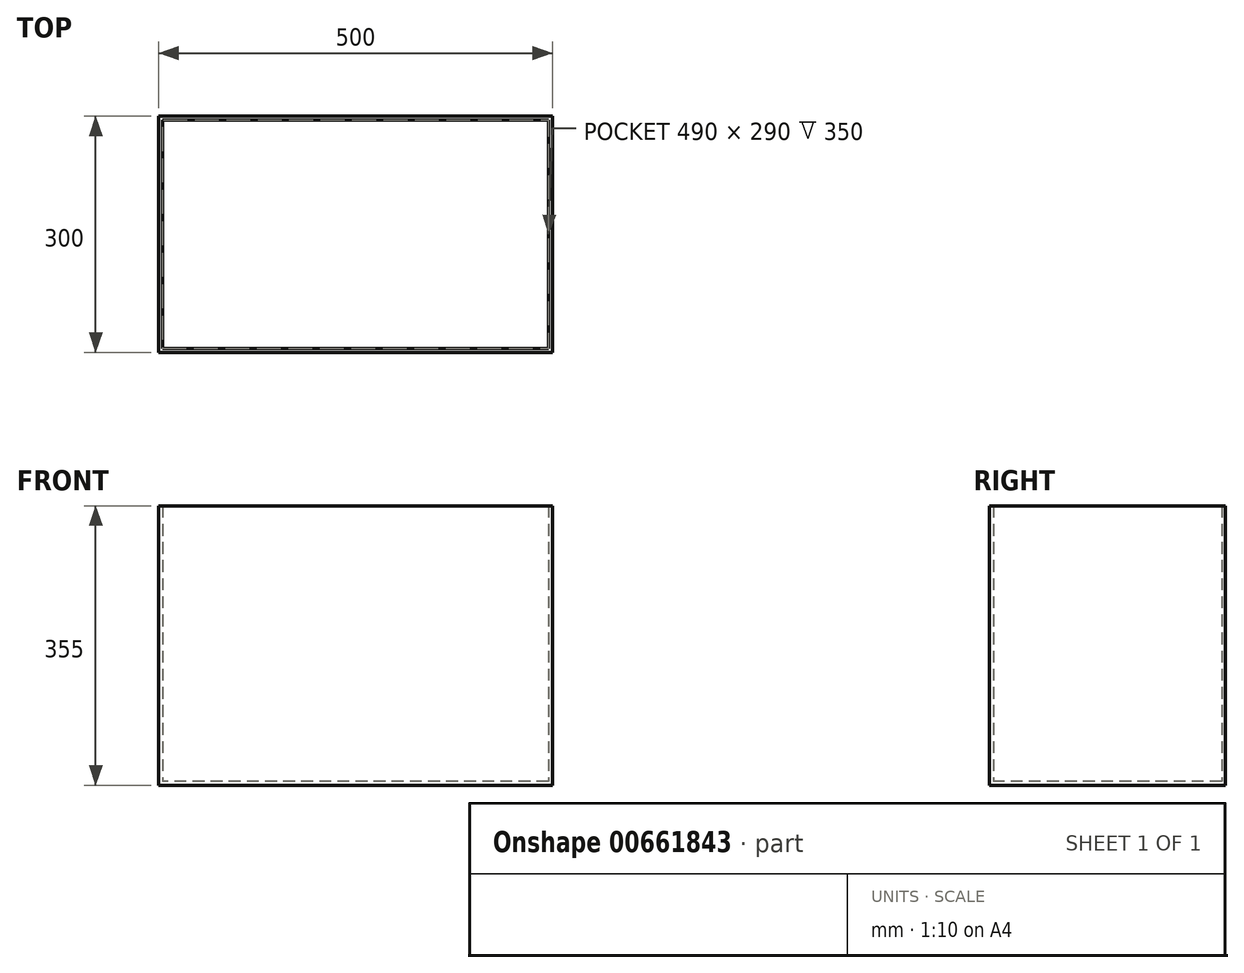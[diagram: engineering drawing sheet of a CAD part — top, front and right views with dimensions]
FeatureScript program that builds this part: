
annotation { "Feature Type Name" : "Feature", "Feature Type Description" : "" }
export const myFeature = defineFeature(function(context is Context, id is Id, definition is map)
    precondition{}
    {
        {
            var Q0;
            Q0=qCreatedBy(makeId("Top.planeOp"),FACE);
            var sketch = newSketch(context, id + "F0", { "sketchPlane" : qUnion([Q0])});
            skLineSegment(sketch, "E0.bottom", {"start": v(250, 150) * mm, "end": v(-250, 150) * mm});
            skLineSegment(sketch, "E0.top", {"start": v(250, -150) * mm, "end": v(-250, -150) * mm});
            skLineSegment(sketch, "E0.left", {"start": v(250, 150) * mm, "end": v(250, -150) * mm});
            skLineSegment(sketch, "E0.right", {"start": v(-250, 150) * mm, "end": v(-250, -150) * mm});
            skPoint(sketch, "E0.middle", {"position": v(0, 0) * mm});
            skLineSegment(sketch, "E1.0", {"start": v(245, 145) * mm, "end": v(-245, 145) * mm});
            skLineSegment(sketch, "E1.1", {"start": v(245, 145) * mm, "end": v(245, -145) * mm});
            skLineSegment(sketch, "E1.2", {"start": v(245, -145) * mm, "end": v(-245, -145) * mm});
            skLineSegment(sketch, "E1.3", {"start": v(-245, 145) * mm, "end": v(-245, -145) * mm});
            skSolve(sketch);
        }
        {
            var Q0;
            Q0=makeQuery(id+"F0.imprint","IMPRINT",FACE,{"disambiguationData":[TD([[makeQuery(id+"F0.imprint","IMPRINT",EDGE,{"derivedFrom":sQuery(id+"F0.wireOp",EDGE,"E1.0")}),1.0]])]});
            var Q1;
            Q1=makeQuery(id+"F0.imprint","IMPRINT",FACE,{"disambiguationData":[TD([[makeQuery(id+"F0.imprint","IMPRINT",EDGE,{"derivedFrom":sQuery(id+"F0.wireOp",EDGE,"E0.bottom")}),1.0]])]});
            extrude(context, id + "F1", {"entities" : qUnion([Q0, Q1]), "oppositeDirection" : true, "depth" : 5 * mm, "offsetDistance" : 25 * mm});
        }
        {
            var Q0;
            Q0=makeQuery(id+"F0.imprint","IMPRINT",FACE,{"disambiguationData":[TD([[makeQuery(id+"F0.imprint","IMPRINT",EDGE,{"derivedFrom":sQuery(id+"F0.wireOp",EDGE,"E0.bottom")}),1.0]])]});
            extrude(context, id + "F2", {"entities" : qUnion([Q0]), "operationType" : NewBodyOperationType.ADD, "depth" : 350 * mm, "offsetDistance" : 25 * mm});
        }
    });
